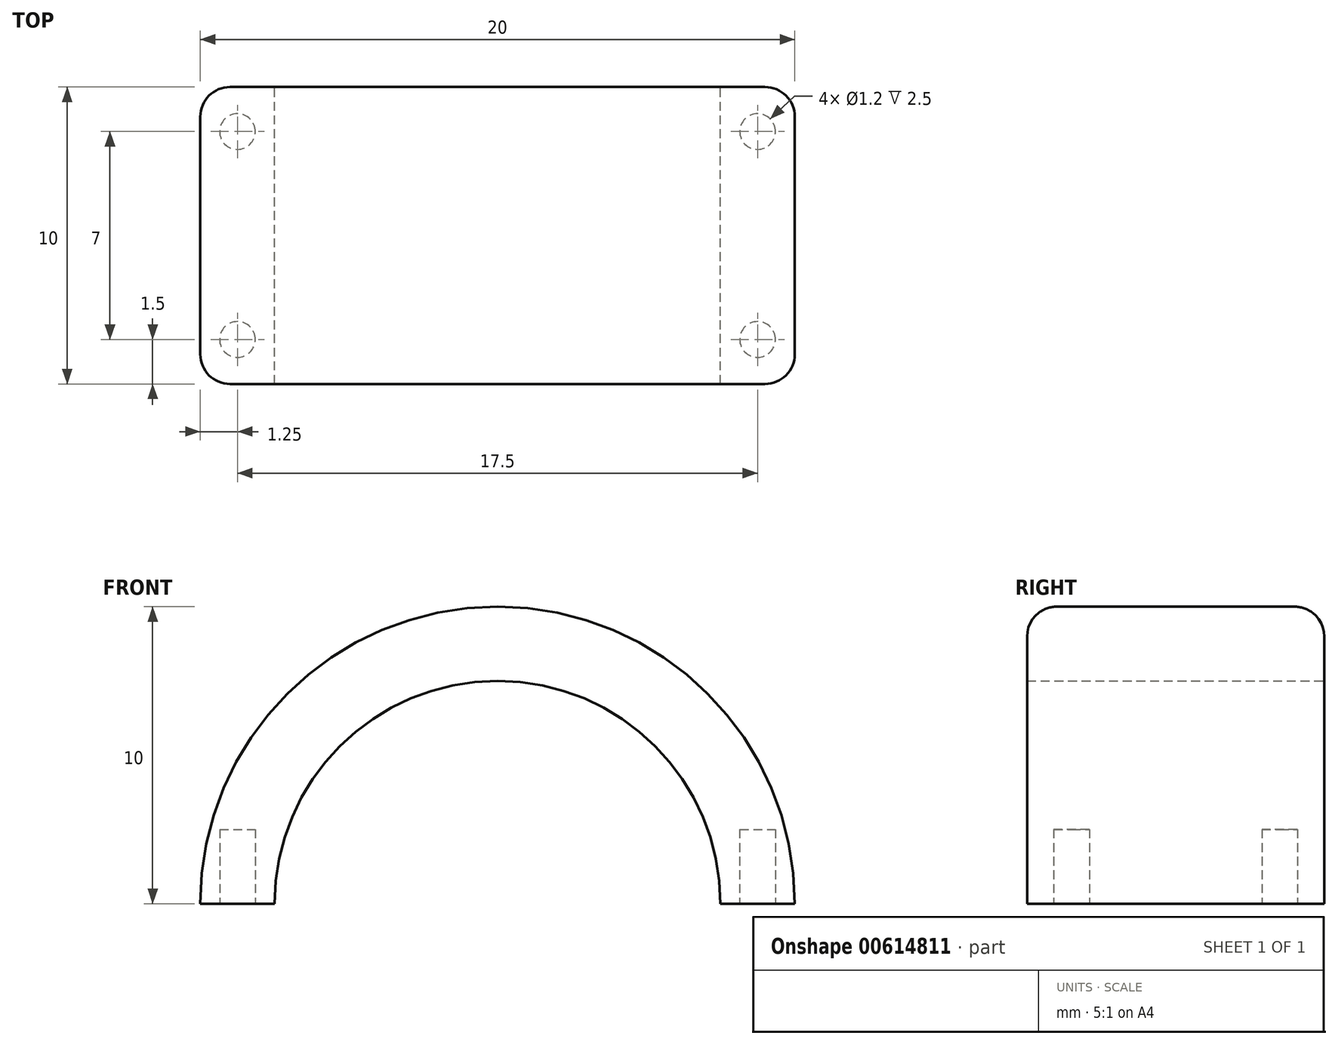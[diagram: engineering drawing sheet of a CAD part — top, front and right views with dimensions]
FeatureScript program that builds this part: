
annotation { "Feature Type Name" : "Feature", "Feature Type Description" : "" }
export const myFeature = defineFeature(function(context is Context, id is Id, definition is map)
    precondition{}
    {
        {
            var Q0;
            Q0=qCreatedBy(makeId("Front.planeOp"),FACE);
            var sketch = newSketch(context, id + "F0", { "sketchPlane" : qUnion([Q0])});
            skArc(sketch, "E0", {"start": v(10, 55.5) * mm, "mid": v(0, 65.5) * mm, "end": v(-10, 55.5) * mm});
            skArc(sketch, "E1", {"start": v(7.5, 55.5) * mm, "mid": v(0, 63) * mm, "end": v(-7.5, 55.5) * mm});
            skLineSegment(sketch, "E2", {"start": v(7.5, 55.5) * mm, "end": v(10, 55.5) * mm});
            skLineSegment(sketch, "E3", {"start": v(10, 55.5) * mm, "end": v(7.5, 55.5) * mm});
            skLineSegment(sketch, "E4", {"start": v(-7.5, 55.5) * mm, "end": v(-10, 55.5) * mm});
            skSolve(sketch);
        }
        {
            var Q0;
            Q0=qSketchRegion(id+"F0",true);
            extrude(context, id + "F1", {"entities" : qUnion([Q0]), "depth" : 10 * mm, "offsetDistance" : 25 * mm});
        }
        {
            var Q0;
            Q0=makeQuery(id+"F1.opExtrude","CAP_EDGE",EDGE,{"disambiguationData":[OSD([sQuery(id+"F0.wireOp",EDGE,"5c7e5983-a695-4cc3-968e-da6723582df20.MirrorCS")])],"isStart":true});
            var Q1;
            Q1=makeQuery(id+"FCyzyHq3IXVLQxi_0.boolean.opBoolean","COPY",EDGE,{"derivedFrom":makeQuery(id+"FCyzyHq3IXVLQxi_0.opExtrude","CAP_EDGE",EDGE,{"disambiguationData":[OSD([sQuery(id+"F0.wireOp",EDGE,"5c7e5983-a695-4cc3-968e-da6723582df20.MirrorCS")])],"isStart":true})});
            var Q2;
            Q2=makeQuery(id+"FCyzyHq3IXVLQxi_0.boolean.opBoolean","COPY",EDGE,{"derivedFrom":makeQuery(id+"FCyzyHq3IXVLQxi_0.opExtrude","CAP_EDGE",EDGE,{"disambiguationData":[OSD([sQuery(id+"F0.wireOp",EDGE,"5c7e5983-a695-4cc3-968e-da6723582df20.MirrorCS")])],"isStart":false})});
            var Q3;
            Q3=makeQuery(id+"F1.opExtrude","CAP_EDGE",EDGE,{"disambiguationData":[OSD([sQuery(id+"F0.wireOp",EDGE,"5c7e5983-a695-4cc3-968e-da6723582df20.MirrorCS")])],"isStart":false});
            var Q4;
            {var subQ0=sQuery(id+"F0.wireOp",EDGE,"CUUYYQxv-gJcw-1UbR-pn1M-oct2M3n5ffUR");Q4=makeQuery(id+"F1.opExtrude","CAP_EDGE",EDGE,{"disambiguationData":[OSD([subQ0]),TDD([makeQuery(id+"F0.imprint","IMPRINT",EDGE,{"disambiguationData":[TD([[makeQuery(id+"F0.imprint","INTERSECT",VERTEX,{"derivedFrom":[subQ0,sQuery(id+"F0.wireOp",EDGE,"5c7e5983-a695-4cc3-968e-da6723582df20.MirrorCS")]}),-1.0]])],"derivedFrom":subQ0})])],"isStart":true});}
            var Q5;
            {var subQ0=sQuery(id+"F0.wireOp",EDGE,"E0");Q5=makeQuery(id+"F1.opExtrude","CAP_EDGE",EDGE,{"disambiguationData":[OSD([subQ0]),TDD([makeQuery(id+"F0.imprint","IMPRINT",EDGE,{"disambiguationData":[TD([[makeQuery(id+"F0.imprint","INTERSECT",VERTEX,{"derivedFrom":[sQuery(id+"F0.wireOp",EDGE,"5c7e5983-a695-4cc3-968e-da6723582df20.MirrorCS"),subQ0]}),1.0]])],"derivedFrom":subQ0})])],"isStart":true});}
            var Q6;
            {var subQ0=sQuery(id+"F0.wireOp",EDGE,"E0");Q6=makeQuery(id+"F1.opExtrude","CAP_EDGE",EDGE,{"disambiguationData":[OSD([subQ0]),TDD([makeQuery(id+"F0.imprint","IMPRINT",EDGE,{"disambiguationData":[TD([[makeQuery(id+"F0.imprint","INTERSECT",VERTEX,{"derivedFrom":[sQuery(id+"F0.wireOp",EDGE,"5c7e5983-a695-4cc3-968e-da6723582df20.MirrorCS"),subQ0]}),1.0]])],"derivedFrom":subQ0})])],"isStart":false});}
            var Q7;
            Q7=makeQuery(id+"F1.opExtrude","CAP_EDGE",EDGE,{"disambiguationData":[OSD([sQuery(id+"F0.wireOp",EDGE,"de459bfc-5631-4295-a9e9-b15d2ce2afe80.MirrorCS")])],"isStart":false});
            var Q8;
            Q8=makeQuery(id+"FCyzyHq3IXVLQxi_0.boolean.opBoolean","COPY",EDGE,{"derivedFrom":makeQuery(id+"FCyzyHq3IXVLQxi_0.opExtrude","CAP_EDGE",EDGE,{"disambiguationData":[OSD([sQuery(id+"F0.wireOp",EDGE,"de459bfc-5631-4295-a9e9-b15d2ce2afe80.MirrorCS")])],"isStart":false})});
            var Q9;
            Q9=makeQuery(id+"FCyzyHq3IXVLQxi_0.boolean.opBoolean","COPY",EDGE,{"derivedFrom":makeQuery(id+"FCyzyHq3IXVLQxi_0.opExtrude","CAP_EDGE",EDGE,{"disambiguationData":[OSD([sQuery(id+"F0.wireOp",EDGE,"de459bfc-5631-4295-a9e9-b15d2ce2afe80.MirrorCS")])],"isStart":true})});
            var Q10;
            Q10=makeQuery(id+"F1.opExtrude","CAP_EDGE",EDGE,{"disambiguationData":[OSD([sQuery(id+"F0.wireOp",EDGE,"de459bfc-5631-4295-a9e9-b15d2ce2afe80.MirrorCS")])],"isStart":true});
            var Q11;
            {var subQ0=sQuery(id+"F0.wireOp",EDGE,"CUUYYQxv-gJcw-1UbR-pn1M-oct2M3n5ffUR");Q11=makeQuery(id+"F1.opExtrude","CAP_EDGE",EDGE,{"disambiguationData":[OSD([subQ0]),TDD([makeQuery(id+"F0.imprint","IMPRINT",EDGE,{"disambiguationData":[TD([[makeQuery(id+"F0.imprint","INTERSECT",VERTEX,{"derivedFrom":[subQ0,sQuery(id+"F0.wireOp",EDGE,"5c7e5983-a695-4cc3-968e-da6723582df20.MirrorCS")]}),-1.0]])],"derivedFrom":subQ0})])],"isStart":false});}
            var Q12;
            Q12=makeQuery(id+"FCyzyHq3IXVLQxi_0.boolean.opBoolean","COPY",EDGE,{"derivedFrom":makeQuery(id+"FCyzyHq3IXVLQxi_0.opExtrude","SWEPT_EDGE",EDGE,{"disambiguationData":[OSD([sQuery(id+"F0.wireOp",EDGE,"E0"),sQuery(id+"F0.wireOp",EDGE,"5f588304-b438-49e0-b1f1-af6acf0aa0a10.MirrorCS")])]})});
            var Q13;
            Q13=makeQuery(id+"FCyzyHq3IXVLQxi_0.boolean.opBoolean","COPY",EDGE,{"derivedFrom":makeQuery(id+"FCyzyHq3IXVLQxi_0.opExtrude","SWEPT_EDGE",EDGE,{"disambiguationData":[OSD([sQuery(id+"F0.wireOp",EDGE,"E0"),sQuery(id+"F0.wireOp",EDGE,"d1077039-0e9e-4d88-8060-094ddf18ddcf.trimOffspring")])]})});
            fillet(context, id + "F2", {"entities" : qUnion([Q0, Q1, Q2, Q3, Q4, Q5, Q6, Q7, Q8, Q9, Q10, Q11, Q12, Q13]), "radius" : 1 * mm, "tangentPropagation" : true, "allowEdgeOverflow" : false});
        }
        {
            var Q0;
            Q0=makeQuery(id+"F1.opExtrude","SWEPT_FACE",FACE,{"disambiguationData":[OSD([sQuery(id+"F0.wireOp",EDGE,"E2")])]});
            var sketch = newSketch(context, id + "F3", { "sketchPlane" : qUnion([Q0])});
            skCircle(sketch, "E5", {"center": v(8.75, 1.5) * mm, "radius": 0.6 * mm});
            skCircle(sketch, "E6", {"center": v(8.75, 8.5) * mm, "radius": 0.6 * mm});
            skCircle(sketch, "E7", {"center": v(-8.75, 1.5) * mm, "radius": 0.6 * mm});
            skCircle(sketch, "E8", {"center": v(-8.75, 8.5) * mm, "radius": 0.6 * mm});
            skLineSegment(sketch, "E9.0", {"start": v(-10, 9) * mm, "end": v(-10, 1) * mm});
            skLineSegment(sketch, "E10.0", {"start": v(-7.5, 10) * mm, "end": v(-7.5, 0) * mm});
            skSolve(sketch);
        }
        {
            var Q0;
            Q0 = qSketchRegion(id + "F3", true);
            extrude(context, id + "F4", {"entities" : qUnion([Q0]), "operationType" : NewBodyOperationType.REMOVE, "oppositeDirection" : true, "depth" : 2.5 * mm, "offsetDistance" : 25 * mm});
        }
    });
